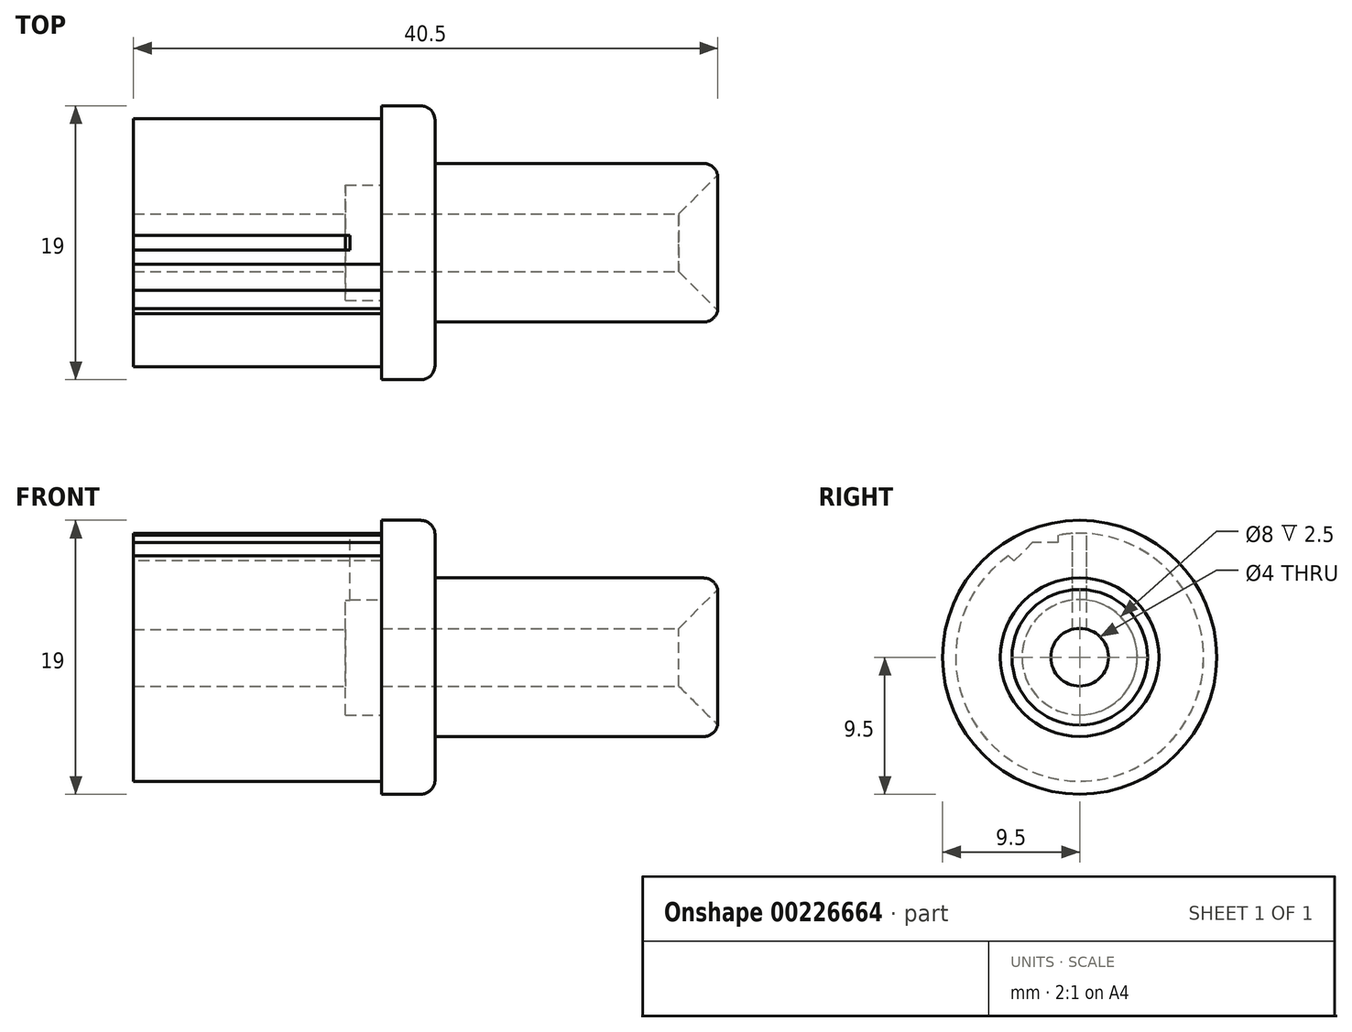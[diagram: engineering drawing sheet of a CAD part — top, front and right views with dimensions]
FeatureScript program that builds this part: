
annotation { "Feature Type Name" : "Feature", "Feature Type Description" : "" }
export const myFeature = defineFeature(function(context is Context, id is Id, definition is map)
    precondition{}
    {
        {
            var Q0;
            Q0=qCreatedBy(makeId("Front.planeOp"),FACE);
            var sketch = newSketch(context, id + "F0", { "sketchPlane" : qUnion([Q0])});
            skLineSegment(sketch, "E0", {"start": v(23.3, 0) * mm, "end": v(23.3, 5.5) * mm});
            skLineSegment(sketch, "E1", {"start": v(23.3, 5.5) * mm, "end": v(3.7, 5.5) * mm});
            skLineSegment(sketch, "E2", {"start": v(3.7, 5.5) * mm, "end": v(3.7, 9.5) * mm});
            skLineSegment(sketch, "E3", {"start": v(3.7, 9.5) * mm, "end": v(0, 9.5) * mm});
            skLineSegment(sketch, "E4", {"start": v(0, 9.5) * mm, "end": v(0, 8.6) * mm});
            skLineSegment(sketch, "E5", {"start": v(0, 8.6) * mm, "end": v(-17.2, 8.6) * mm});
            skLineSegment(sketch, "E6", {"start": v(-17.2, 8.6) * mm, "end": v(-17.2, 0) * mm});
            skLineSegment(sketch, "E7", {"start": v(-17.2, 0) * mm, "end": v(23.3, 0) * mm});
            skSolve(sketch);
        }
        {
            var Q0;
            Q0=qCreatedBy(makeId("Front.planeOp"),FACE);
            var sketch = newSketch(context, id + "F1", { "sketchPlane" : qUnion([Q0])});
            skLineSegment(sketch, "E8", {"start": v(-24.95, 0) * mm, "end": v(32.3, 0) * mm, "construction": true});
            skSolve(sketch);
        }
        {
            var Q0;
            Q0=makeQuery(id+"F0.imprint","IMPRINT",FACE,{"disambiguationData":[TD([[makeQuery(id+"F0.imprint","IMPRINT",EDGE,{"derivedFrom":sQuery(id+"F0.wireOp",EDGE,"E0")}),1.0]])]});
            var Q1;
            Q1=sQuery(id+"F1.wireOp",EDGE,"E8");
            revolve(context, id + "F2", {"entities" : qUnion([Q0]), "axis" : qUnion([Q1]), "revolveType" : RevolveType.FULL});
        }
        {
            var Q0;
            Q0=qCreatedBy(makeId("Front.planeOp"),FACE);
            var sketch = newSketch(context, id + "F3", { "sketchPlane" : qUnion([Q0])});
            skLineSegment(sketch, "E9", {"start": v(23.3, 0) * mm, "end": v(23.3, 4.7) * mm});
            skLineSegment(sketch, "E10", {"start": v(23.3, 4.7) * mm, "end": v(20.6, 2) * mm});
            skLineSegment(sketch, "E11", {"start": v(20.6, 2) * mm, "end": v(0, 2) * mm});
            skLineSegment(sketch, "E12", {"start": v(0, 2) * mm, "end": v(0, 4) * mm});
            skLineSegment(sketch, "E13", {"start": v(0, 4) * mm, "end": v(-2.5, 4) * mm});
            skLineSegment(sketch, "E14", {"start": v(-2.5, 4) * mm, "end": v(-2.5, 2) * mm});
            skLineSegment(sketch, "E15", {"start": v(-2.5, 2) * mm, "end": v(-17.2, 2) * mm});
            skLineSegment(sketch, "E16", {"start": v(-17.2, 2) * mm, "end": v(-17.2, 0) * mm});
            skLineSegment(sketch, "E17", {"start": v(-17.2, 0) * mm, "end": v(23.3, 0) * mm});
            skSolve(sketch);
        }
        {
            var Q0;
            Q0 = qSketchRegion(id + "F3", true);
            var Q1;
            Q1=sQuery(id+"F3.wireOp",EDGE,"E17");
            revolve(context, id + "F4", {"operationType" : NewBodyOperationType.REMOVE, "entities" : qUnion([Q0]), "axis" : qUnion([Q1]), "revolveType" : RevolveType.FULL, "oppositeDirection" : true});
        }
        {
            var Q0;
            Q0=makeQuery(id+"F2.opRevolve","SWEPT_FACE",FACE,{"disambiguationData":[OSD([sQuery(id+"F0.wireOp",EDGE,"E6")])]});
            var sketch = newSketch(context, id + "F5", { "sketchPlane" : qUnion([Q0])});
            skLineSegment(sketch, "E18.bottom", {"start": v(-0.5, 0) * mm, "end": v(0.5, 0) * mm});
            skLineSegment(sketch, "E18.top", {"start": v(-0.5, 9) * mm, "end": v(0.5, 9) * mm});
            skLineSegment(sketch, "E18.left", {"start": v(-0.5, 0) * mm, "end": v(-0.5, 9) * mm});
            skLineSegment(sketch, "E18.right", {"start": v(0.5, 0) * mm, "end": v(0.5, 9) * mm});
            skSolve(sketch);
        }
        {
            var Q0;
            Q0 = qSketchRegion(id + "F5", true);
            extrude(context, id + "F6", {"entities" : qUnion([Q0]), "operationType" : NewBodyOperationType.REMOVE, "oppositeDirection" : true, "depth" : 15 * mm});
        }
        {
            var Q0;
            Q0=makeQuery(id+"Fy3Br13UPA26ZbM_1.1.F6.boolean.opBoolean","SPLIT",FACE,{"disambiguationData":[TD([makeQuery(id+"F6.boolean.opBoolean","COPY",FACE,{"derivedFrom":makeQuery(id+"F6.opExtrude","SWEPT_FACE",FACE,{"disambiguationData":[OSD([sQuery(id+"F5.wireOp",EDGE,"E18.right")])]})})])],"derivedFrom":makeQuery(id+"F2.opRevolve","SWEPT_FACE",FACE,{"disambiguationData":[OSD([sQuery(id+"F0.wireOp",EDGE,"E6")])]})});
            var sketch = newSketch(context, id + "F7", { "sketchPlane" : qUnion([Q0])});
            skLineSegment(sketch, "E19.bottom", {"start": v(1.5, 9.95) * mm, "end": v(3.3, 9.95) * mm});
            skLineSegment(sketch, "E19.top", {"start": v(1.5, 7.95) * mm, "end": v(3.3, 7.95) * mm});
            skLineSegment(sketch, "E19.left", {"start": v(1.5, 9.95) * mm, "end": v(1.5, 7.95) * mm});
            skLineSegment(sketch, "E19.right", {"start": v(3.3, 9.95) * mm, "end": v(3.3, 7.95) * mm});
            skLineSegment(sketch, "E20", {"start": v(0, 0) * mm, "end": v(3.3, 7.95) * mm, "construction": true});
            skLineSegment(sketch, "E21.MirrorCS", {"start": v(4.56, 6.68) * mm, "end": v(3.3, 7.95) * mm});
            skLineSegment(sketch, "E22.MirrorCS", {"start": v(5.97, 8.1) * mm, "end": v(4.7, 9.36) * mm});
            skLineSegment(sketch, "E23.MirrorCS", {"start": v(4.7, 9.36) * mm, "end": v(3.3, 7.95) * mm});
            skLineSegment(sketch, "E24.MirrorCS", {"start": v(5.97, 8.1) * mm, "end": v(4.56, 6.68) * mm});
            skSolve(sketch);
        }
        {
            var Q0;
            Q0 = qSketchRegion(id + "F7", true);
            var Q1;
            Q1=makeQuery(id+"F2.opRevolve","SWEPT_FACE",FACE,{"disambiguationData":[OSD([sQuery(id+"F0.wireOp",EDGE,"E4")])]});
            extrude(context, id + "F8", {"entities" : qUnion([Q0]), "operationType" : NewBodyOperationType.REMOVE, "endBound" : BoundingType.UP_TO_SURFACE, "oppositeDirection" : true, "endBoundEntityFace" : qUnion([Q1]), "depth" : 25 * mm});
        }
        {
            var Q0;
            Q0=makeQuery(id+"F2.opRevolve","SWEPT_EDGE",EDGE,{"disambiguationData":[OSD([sQuery(id+"F0.wireOp",EDGE,"E0"),sQuery(id+"F0.wireOp",EDGE,"E1")])]});
            var Q1;
            Q1=makeQuery(id+"F2.opRevolve","SWEPT_EDGE",EDGE,{"disambiguationData":[OSD([sQuery(id+"F0.wireOp",EDGE,"E2"),sQuery(id+"F0.wireOp",EDGE,"E3")])]});
            fillet(context, id + "F9", {"entities" : qUnion([Q0, Q1]), "radius" : 1 * mm, "tangentPropagation" : true, "allowEdgeOverflow" : false});
        }
    });
